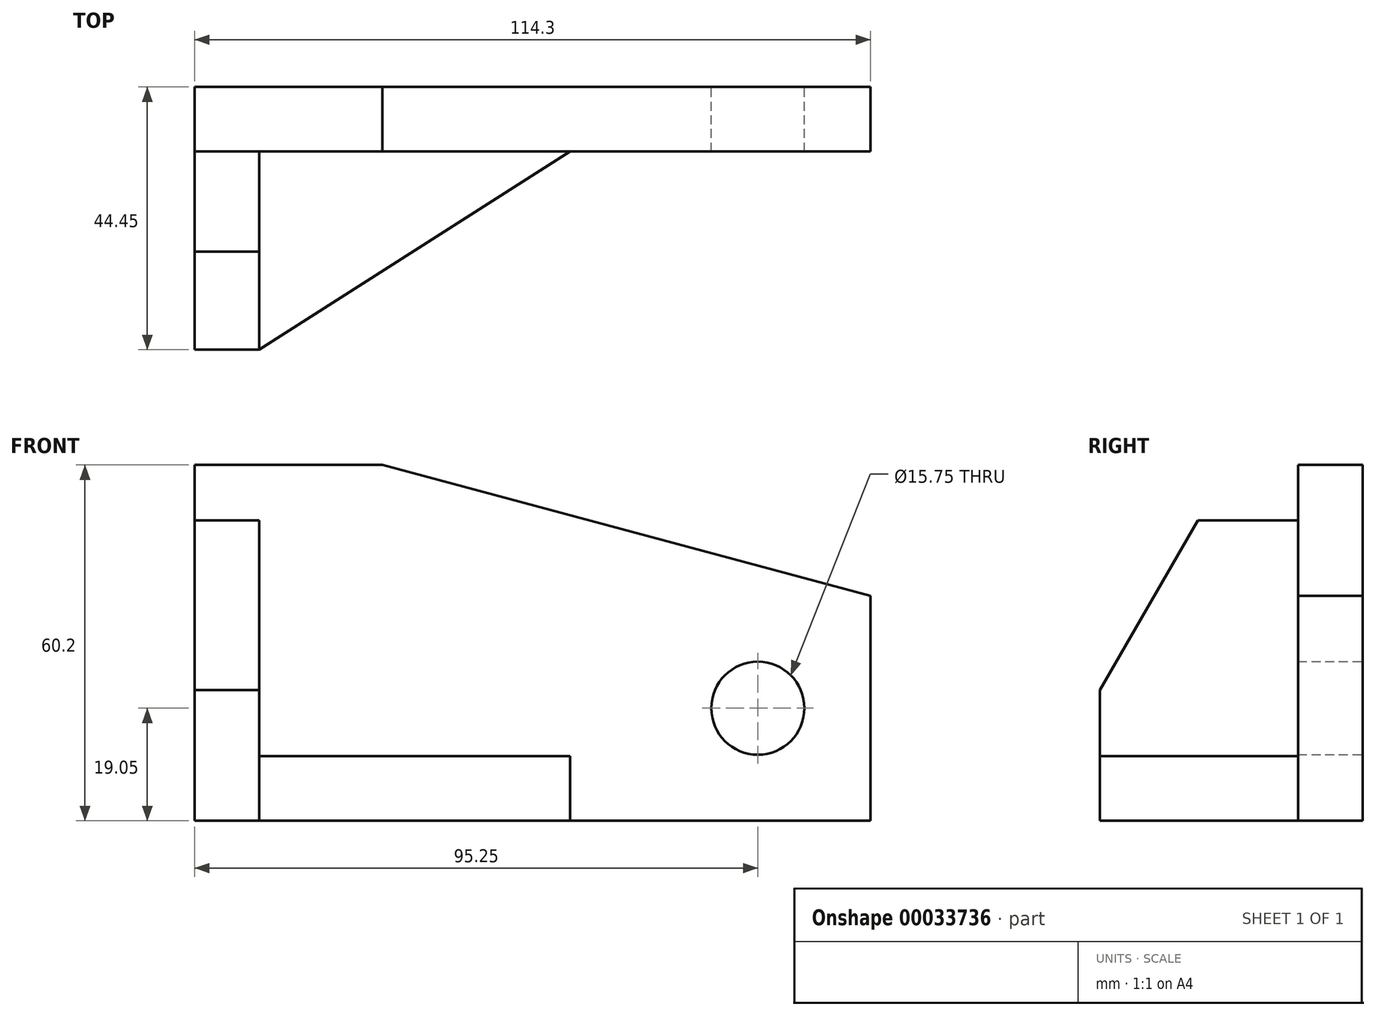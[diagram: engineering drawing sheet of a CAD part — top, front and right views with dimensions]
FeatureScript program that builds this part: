
annotation { "Feature Type Name" : "Feature", "Feature Type Description" : "" }
export const myFeature = defineFeature(function(context is Context, id is Id, definition is map)
    precondition{}
    {
        {
            var Q0;
            Q0=qCreatedBy(makeId("Front.planeOp"),FACE);
            var sketch = newSketch(context, id + "F0", { "sketchPlane" : qUnion([Q0])});
            skLineSegment(sketch, "E0.bottom", {"start": v(0, 0) * mm, "end": v(-114.3, 0) * mm});
            skLineSegment(sketch, "E0.top", {"start": v(0, 60.2) * mm, "end": v(-114.3, 60.2) * mm});
            skLineSegment(sketch, "E0.left", {"start": v(0, 0) * mm, "end": v(0, 60.2) * mm});
            skLineSegment(sketch, "E0.right", {"start": v(-114.3, 0) * mm, "end": v(-114.3, 60.2) * mm});
            skLineSegment(sketch, "E1", {"start": v(-82.55, 60.2) * mm, "end": v(0, 38.08) * mm});
            skCircle(sketch, "E2", {"center": v(-19.05, 19.05) * mm, "radius": 7.87 * mm});
            skSolve(sketch);
        }
        {
            var Q0;
            {var subQ3=sQuery(id+"F0.wireOp",EDGE,"E0.bottom");Q0=makeQuery(id+"F0.imprint","IMPRINT",FACE,{"disambiguationData":[TD([[makeQuery(id+"F0.imprint","IMPRINT",EDGE,{"derivedFrom":subQ3}),-1.0]])]});}
            extrude(context, id + "F1", {"entities" : qUnion([Q0]), "depth" : 10.92 * mm});
        }
        {
            var Q0;
            Q0=makeQuery(id+"F1.opExtrude","SWEPT_FACE",FACE,{"disambiguationData":[OSD([sQuery(id+"F0.wireOp",EDGE,"E0.right")])]});
            var sketch = newSketch(context, id + "F2", { "sketchPlane" : qUnion([Q0])});
            skLineSegment(sketch, "E3.bottom", {"start": v(10.92, 0) * mm, "end": v(44.45, 0) * mm});
            skLineSegment(sketch, "E3.top", {"start": v(10.92, 50.8) * mm, "end": v(44.45, 50.8) * mm});
            skLineSegment(sketch, "E3.left", {"start": v(10.92, 0) * mm, "end": v(10.92, 50.8) * mm});
            skLineSegment(sketch, "E3.right", {"start": v(44.45, 0) * mm, "end": v(44.45, 50.8) * mm});
            skLineSegment(sketch, "E4", {"start": v(27.88, 50.8) * mm, "end": v(44.45, 22.1) * mm});
            skSolve(sketch);
        }
        {
            var Q0;
            {var subQ2=sQuery(id+"F2.wireOp",EDGE,"E3.bottom");Q0=makeQuery(id+"F2.imprint","IMPRINT",FACE,{"disambiguationData":[TD([[makeQuery(id+"F2.imprint","IMPRINT",EDGE,{"derivedFrom":subQ2}),1.0]])]});}
            extrude(context, id + "F3", {"entities" : qUnion([Q0]), "operationType" : NewBodyOperationType.ADD, "oppositeDirection" : true, "depth" : 10.92 * mm});
        }
        {
            var Q0;
            Q0=makeQuery(id+"F3.boolean.opBoolean","MERGE",FACE,{"derivedFrom":[makeQuery(id+"F1.opExtrude","SWEPT_FACE",FACE,{"disambiguationData":[OSD([sQuery(id+"F0.wireOp",EDGE,"E0.bottom")])]}),makeQuery(id+"F3.opExtrude","SWEPT_FACE",FACE,{"disambiguationData":[OSD([sQuery(id+"F2.wireOp",EDGE,"E3.bottom")])]})]});
            var sketch = newSketch(context, id + "F4", { "sketchPlane" : qUnion([Q0])});
            skLineSegment(sketch, "E5", {"start": v(-103.38, 44.45) * mm, "end": v(-50.8, 10.92) * mm});
            skSolve(sketch);
        }
        {
            var Q0;
            {var subQ1=sQuery(id+"F4.wireOp",EDGE,"E5");Q0=makeQuery(id+"F4.imprint","IMPRINT",FACE,{"disambiguationData":[TD([[makeQuery(id+"F4.imprint","IMPRINT",EDGE,{"derivedFrom":subQ1}),-1.0]])]});}
            extrude(context, id + "F5", {"entities" : qUnion([Q0]), "operationType" : NewBodyOperationType.ADD, "oppositeDirection" : true, "depth" : 10.92 * mm});
        }
    });
